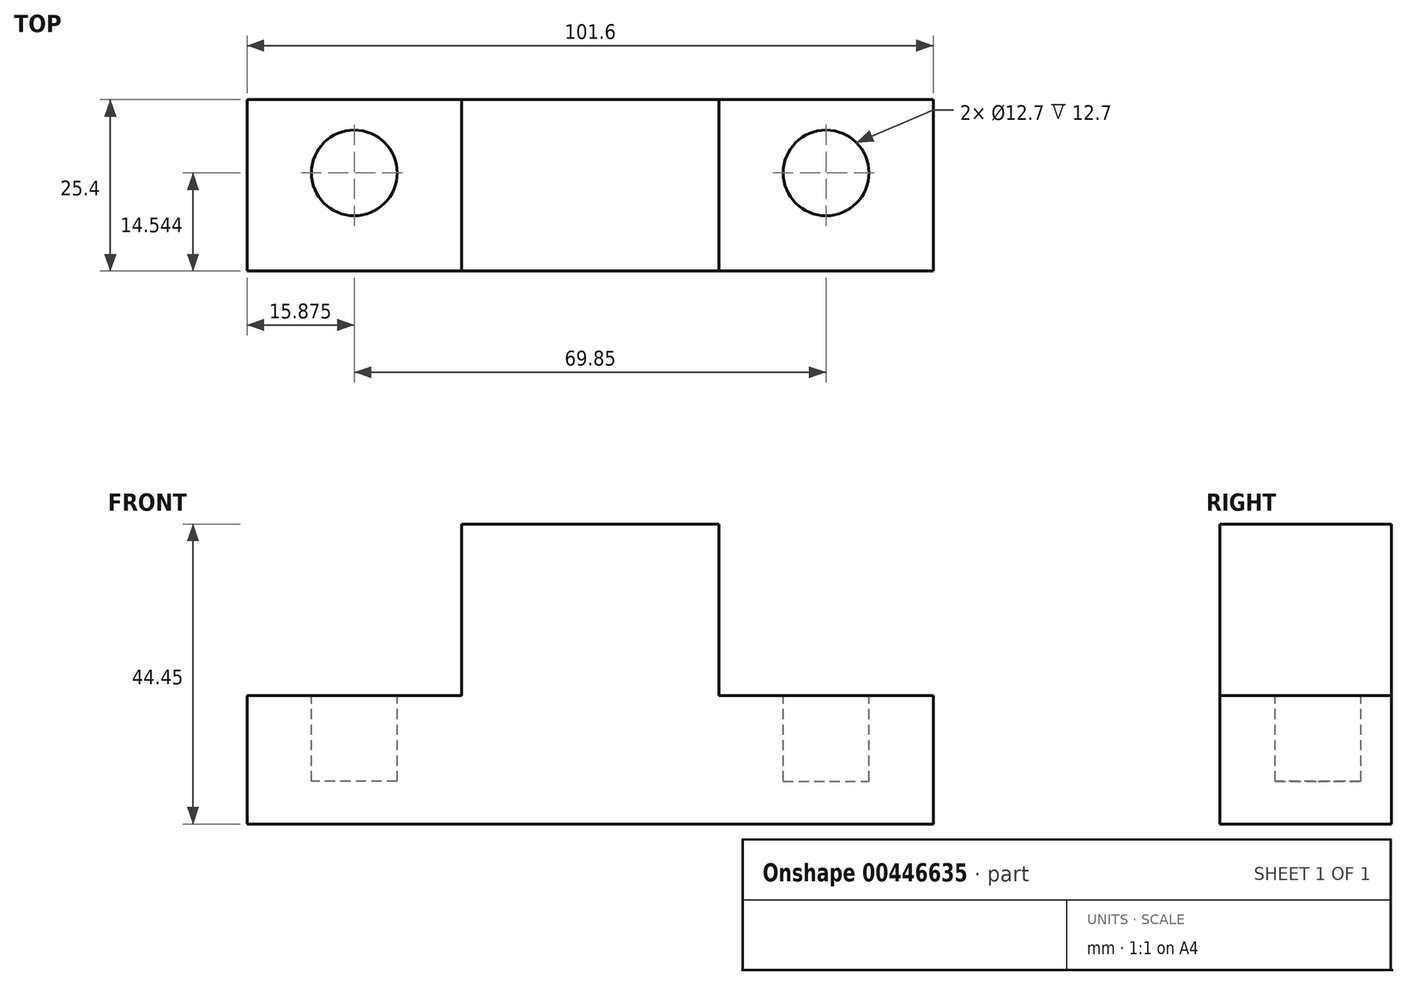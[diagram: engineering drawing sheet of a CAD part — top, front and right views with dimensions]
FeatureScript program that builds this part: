
annotation { "Feature Type Name" : "Feature", "Feature Type Description" : "" }
export const myFeature = defineFeature(function(context is Context, id is Id, definition is map)
    precondition{}
    {
        {
            var Q0;
            Q0=qCreatedBy(makeId("Front.planeOp"),FACE);
            var sketch = newSketch(context, id + "F0", { "sketchPlane" : qUnion([Q0])});
            skLineSegment(sketch, "E0", {"start": v(-19.05, 0) * mm, "end": v(-19.05, -25.4) * mm});
            skLineSegment(sketch, "E1", {"start": v(-19.05, -25.4) * mm, "end": v(-50.8, -25.4) * mm});
            skLineSegment(sketch, "E2", {"start": v(-50.8, -25.4) * mm, "end": v(-50.8, -44.45) * mm});
            skLineSegment(sketch, "E3", {"start": v(-50.8, -44.45) * mm, "end": v(0, -44.45) * mm});
            skLineSegment(sketch, "E4", {"start": v(0, -44.45) * mm, "end": v(0, 0) * mm});
            skLineSegment(sketch, "E5", {"start": v(0, 0) * mm, "end": v(-19.05, 0) * mm});
            skSolve(sketch);
        }
        {
            var Q0;
            Q0 = qSketchRegion(id + "F0", true);
            extrude(context, id + "F1", {"entities" : qUnion([Q0]), "depth" : 25.4 * mm});
        }
        {
            var Q0;
            Q0=makeQuery(id+"F1.opExtrude","SWEPT_FACE",FACE,{"disambiguationData":[OSD([sQuery(id+"F0.wireOp",EDGE,"E1")])]});
            var sketch = newSketch(context, id + "F2", { "sketchPlane" : qUnion([Q0])});
            skCircle(sketch, "E6", {"center": v(-34.92, -10.86) * mm, "radius": 6.35 * mm});
            skPoint(sketch, "E6.centerSnap0", {"position": v(-34.92, -25.4) * mm});
            skSolve(sketch);
        }
        {
            var Q0;
            Q0 = qSketchRegion(id + "F2", true);
            extrude(context, id + "F3", {"entities" : qUnion([Q0]), "operationType" : NewBodyOperationType.REMOVE, "oppositeDirection" : true, "depth" : 12.7 * mm});
        }
        {
            var Q0;
            Q0=makeQuery(id+"F1.opExtrude","SWEPT_BODY",BODY,{"disambiguationData":[OSD([sQuery(id+"F0.wireOp",EDGE,"E0"),sQuery(id+"F0.wireOp",EDGE,"E1"),sQuery(id+"F0.wireOp",EDGE,"E2"),sQuery(id+"F0.wireOp",EDGE,"E3"),sQuery(id+"F0.wireOp",EDGE,"E4"),sQuery(id+"F0.wireOp",EDGE,"E5")])]});
            var Q1;
            Q1=qCreatedBy(makeId("Right.planeOp"),FACE);
            mirror(context, id + "F4", {"operationType" : NewBodyOperationType.ADD, "entities" : qUnion([Q0]), "mirrorPlane" : qUnion([Q1])});
        }
    });
